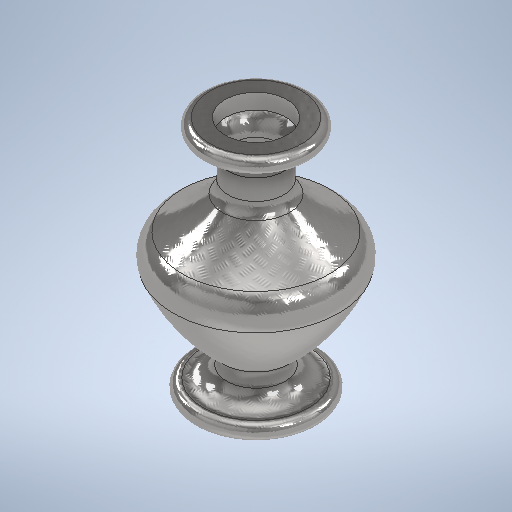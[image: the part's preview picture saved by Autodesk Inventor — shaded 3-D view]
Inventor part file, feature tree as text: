
AUTODESK INVENTOR PART (.ipt)
format: ipt  version: 2025.2 (Build 292293000, 293)  size: 669,696 bytes
history: native  units: in
note: dims shown in document units (in); Inventor stores cm internally (conversion verified against a paired STEP export)
features: revolve x1, sketch x1, other x1
ambient origin geometry x8: Origin, YZ Plane, XZ Plane, XY Plane, X Axis, Y Axis, Z Axis, Center Point
bodies: Solid1 (feature_tree)
feature tree (3):
  revolve  "Revolution1"  [1 undecoded]
  sketch  "Sketch1"  dims[d12=0.1969in d21=0.7087in d24=0.3937in d25=1.2598in d26=2.3504in d27=4.9134in d32=0.9449in d33=0.5394in d34=0.9449in d36=0.6575in d39=0.1575in d43=90.0deg]
  other  "Image1"
note: 1 required parameter value undecoded (feature->parameter linkage not recoverable at this tier; creation-order binding heuristic only, values carry confidence <= 0.55)
